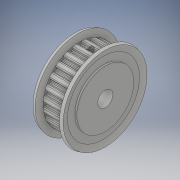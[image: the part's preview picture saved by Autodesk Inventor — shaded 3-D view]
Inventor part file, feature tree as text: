
AUTODESK INVENTOR PART (.ipt)
format: ipt  version: 2019 (Build 230136000, 136)  size: 539,136 bytes
history: native  units: mm
features: other x14, revolve x3, thread x2, hole x1, extrude x1, sketch x1
ambient origin geometry x8: Origin, YZ Plane, XZ Plane, XY Plane, X Axis, Y Axis, Z Axis, Center Point
bodies: Solid1 (feature_tree)
feature tree (22):
  revolve  "Revolution1"  [1 undecoded]
  hole  "Hole1"  [1 undecoded]
  extrude  "Extrusion1"  Depth=15.15mm TaperAngle=0.0deg
  revolve  "Revolution2"  Angle=360.0deg
  thread  "Thread1"  [1 undecoded]
  revolve  "Revolution3"  [1 undecoded]
  thread  "Thread2"  [1 undecoded]
  other  "to_screw1_XY"
  other  "to_screw1_YZ"
  other  "to_screw1_ZX"
  other  "to_screw1_X"
  other  "to_screw1_Y"
  other  "to_screw1_Z"
  other  "to_screw1_Center"
  other  "to_screw2_XY"
  other  "to_screw2_YZ"
  other  "to_screw2_ZX"
  other  "to_screw2_X"
  other  "to_screw2_Y"
  other  "to_screw2_Z"
  other  "to_screw2_Center"
  sketch  "Sketch2"  dims[d0=360.0deg d1=8.0mm d2=6.0mm d3=4.0mm d4=2.0mm d5=90.0deg d6=16.0mm d7=0.0mm d8=11.0mm d9=0.0mm d10=360.0deg d11=15.15mm d12=0.0mm d13=360.0deg d14=15.15mm d15=0.0mm]
note: 5 required parameter values undecoded (feature->parameter linkage not recoverable at this tier; creation-order binding heuristic only, values carry confidence <= 0.55)